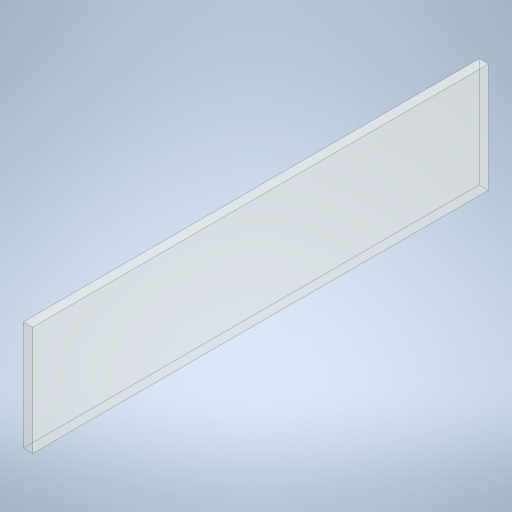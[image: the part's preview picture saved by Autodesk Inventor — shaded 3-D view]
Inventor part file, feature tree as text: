
AUTODESK INVENTOR PART (.ipt)
format: ipt  version: 2024 (Build 280153000, 153)  size: 229,376 bytes
history: native  units: in
note: dims shown in document units (in); Inventor stores cm internally (conversion verified against a paired STEP export)
features: extrude x1, sketch x1
ambient origin geometry x8: Origin, YZ Plane, XZ Plane, XY Plane, X Axis, Y Axis, Z Axis, Center Point
bodies: Body1 (feature_tree)
feature tree (2):
  extrude  "Extrusion3"  Depth=7.7165in
  sketch  "Sketch3"  dims[d8=1.8504in d9=7.7165in d10=0.1575in d11=0.0in]
